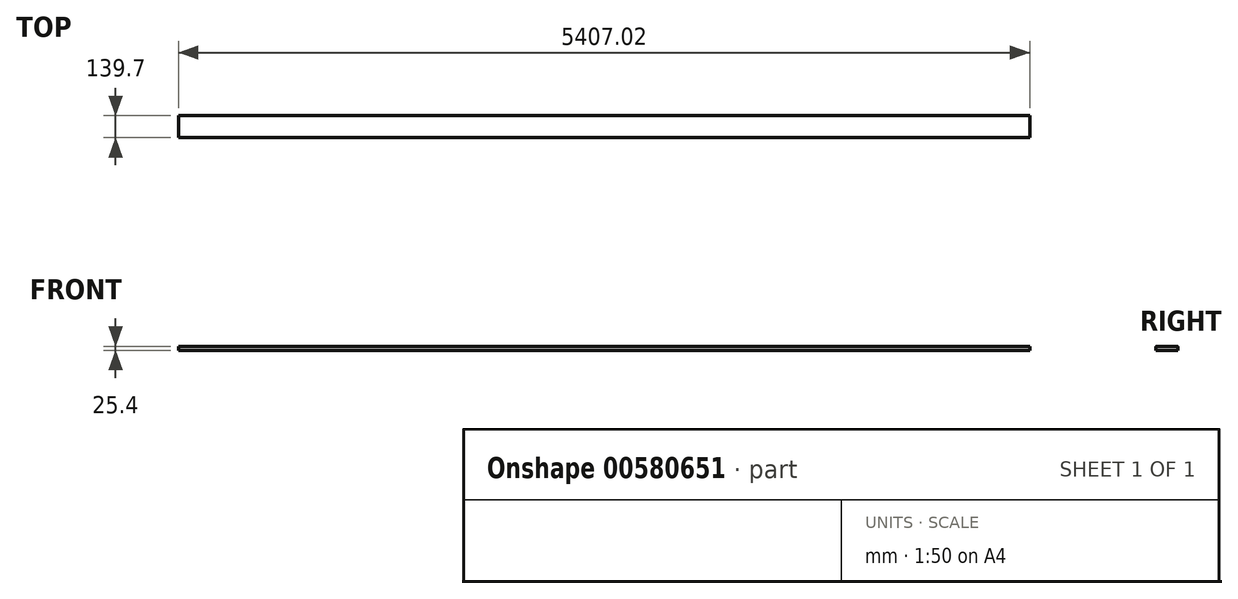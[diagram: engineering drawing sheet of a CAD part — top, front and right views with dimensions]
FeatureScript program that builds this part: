
annotation { "Feature Type Name" : "Feature", "Feature Type Description" : "" }
export const myFeature = defineFeature(function(context is Context, id is Id, definition is map)
    precondition{}
    {
        {
            var Q0;
            Q0=qCreatedBy(makeId("Top.planeOp"),FACE);
            var sketch = newSketch(context, id + "F0", { "sketchPlane" : qUnion([Q0])});
            skLineSegment(sketch, "E0.bottom", {"start": v(2703.51, -69.85) * mm, "end": v(-2703.51, -69.85) * mm});
            skLineSegment(sketch, "E0.top", {"start": v(2703.51, 69.85) * mm, "end": v(-2703.51, 69.85) * mm});
            skLineSegment(sketch, "E0.left", {"start": v(2703.51, -69.85) * mm, "end": v(2703.51, 69.85) * mm});
            skLineSegment(sketch, "E0.right", {"start": v(-2703.51, -69.85) * mm, "end": v(-2703.51, 69.85) * mm});
            skPoint(sketch, "E0.middle", {"position": v(0, 0) * mm});
            skSolve(sketch);
        }
        {
            var Q0;
            Q0=makeQuery(id+"F0.imprint","IMPRINT",FACE,{"disambiguationData":[TD([[makeQuery(id+"F0.imprint","IMPRINT",EDGE,{"derivedFrom":sQuery(id+"F0.wireOp",EDGE,"E0.bottom")}),-1.0]])]});
            extrude(context, id + "F1", {"entities" : qUnion([Q0]), "depth" : 25.4 * mm, "offsetDistance" : 25.4 * mm});
        }
        {
            var Q0;
            Q0=makeQuery(id+"F1.opExtrude","CAP_EDGE",EDGE,{"disambiguationData":[OSD([sQuery(id+"F0.wireOp",EDGE,"E0.top")])],"isStart":false});
            var Q1;
            Q1=makeQuery(id+"F1.opExtrude","CAP_EDGE",EDGE,{"disambiguationData":[OSD([sQuery(id+"F0.wireOp",EDGE,"E0.bottom")])],"isStart":false});
            fillet(context, id + "F2", {"entities" : qUnion([Q0, Q1]), "radius" : 5.08 * mm, "tangentPropagation" : true, "allowEdgeOverflow" : false});
        }
    });
